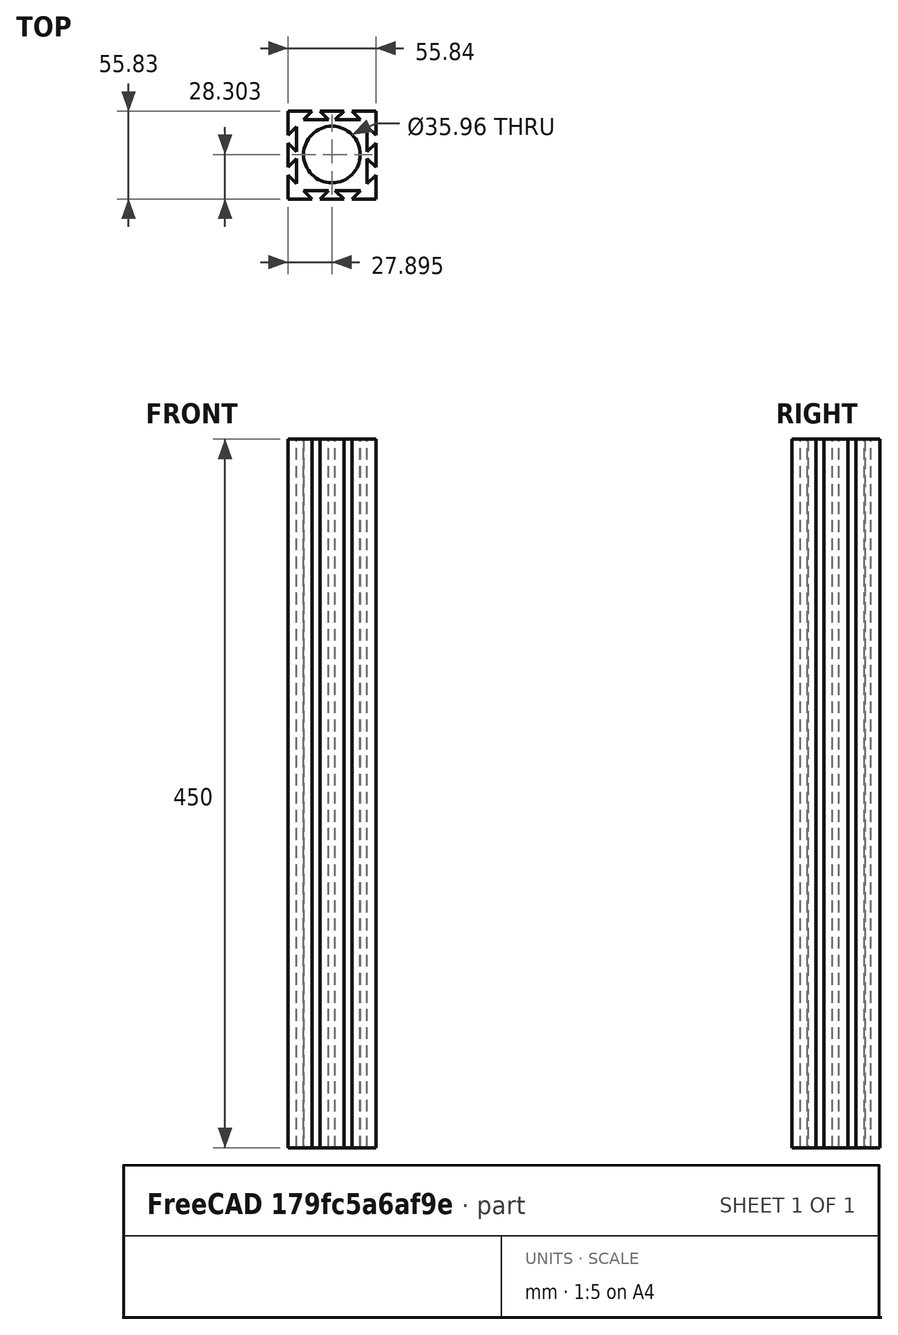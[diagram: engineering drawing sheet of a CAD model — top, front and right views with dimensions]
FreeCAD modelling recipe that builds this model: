
FCSTD DOCUMENT  (FreeCAD 0.18R16110 (Git))
Label: Quadextrusion
License: All rights reserved
LicenseURL: http://en.wikipedia.org/wiki/All_rights_reserved
objects: Sketcher::SketchObject×1, Part::Extrusion×1
note: 2 computed .brp shape members not serialized (recipe doc carries the construction recipe); baked Part::Feature solids carry a one-line shape summary decoded from their .brp

FEATURE [Sketcher::SketchObject] Sketch
  sketch-geometry (62):
    g0: LineSegment StartX=81.5164 StartY=-47.279 StartZ=0 EndX=81.5164 EndY=-62.5946 EndZ=0
    g1: LineSegment StartX=81.5164 StartY=-62.5946 StartZ=0 EndX=66.2008 EndY=-62.5946 EndZ=0
    g2: LineSegment StartX=66.2008 StartY=-62.5946 StartZ=0 EndX=71.7008 EndY=-57.0946 EndZ=0
    g3: LineSegment StartX=71.7008 StartY=-57.0946 StartZ=0 EndX=55.7008 EndY=-57.0946 EndZ=0
    g4: LineSegment StartX=55.7008 StartY=-57.0946 StartZ=0 EndX=61.2008 EndY=-62.5946 EndZ=0
    g5: LineSegment StartX=61.2008 StartY=-62.5946 StartZ=0 EndX=45.9941 EndY=-62.5946 EndZ=0
    g6: LineSegment [constr] StartX=61.2008 StartY=-62.5946 StartZ=0 EndX=66.2008 EndY=-62.5946 EndZ=0
    g7: LineSegment [constr] StartX=55.7008 StartY=-57.0946 StartZ=0 EndX=55.7008 EndY=-62.5946 EndZ=0
    g8: LineSegment StartX=81.5164 StartY=-47.279 StartZ=0 EndX=76.0164 EndY=-52.779 EndZ=0
    g9: LineSegment StartX=76.0164 StartY=-52.779 StartZ=0 EndX=76.0164 EndY=-36.779 EndZ=0
    g10: LineSegment StartX=76.0164 StartY=-36.779 StartZ=0 EndX=81.5164 EndY=-42.279 EndZ=0
    g11: LineSegment StartX=81.5164 StartY=-42.279 StartZ=0 EndX=81.5164 EndY=-27.0723 EndZ=0
    g12: LineSegment StartX=45.9941 StartY=-62.5946 StartZ=0 EndX=51.4941 EndY=-57.0946 EndZ=0
    g13: LineSegment StartX=51.4941 StartY=-57.0946 StartZ=0 EndX=35.4941 EndY=-57.0946 EndZ=0
    g14: LineSegment StartX=35.4941 StartY=-57.0946 StartZ=0 EndX=40.9941 EndY=-62.5946 EndZ=0
    g15: LineSegment StartX=40.9941 StartY=-62.5946 StartZ=0 EndX=25.6785 EndY=-62.5946 EndZ=0
    g16: LineSegment StartX=25.6785 StartY=-62.5946 StartZ=0 EndX=25.6785 EndY=-47.279 EndZ=0
    g17: LineSegment [constr] StartX=35.4941 StartY=-57.0946 StartZ=0 EndX=35.4941 EndY=-62.5946 EndZ=0
    g18: LineSegment [constr] StartX=40.9941 StartY=-62.5946 StartZ=0 EndX=45.9941 EndY=-62.5946 EndZ=0
    g19: LineSegment StartX=81.5164 StartY=-27.0723 StartZ=0 EndX=76.0164 EndY=-32.5723 EndZ=0
    g20: LineSegment StartX=76.0164 StartY=-32.5723 StartZ=0 EndX=76.0164 EndY=-16.5723 EndZ=0
    g21: LineSegment StartX=76.0164 StartY=-16.5723 StartZ=0 EndX=81.5164 EndY=-22.0723 EndZ=0
    g22: LineSegment StartX=81.5164 StartY=-22.0723 StartZ=0 EndX=81.5164 EndY=-6.75669 EndZ=0
    g23: LineSegment StartX=81.5164 StartY=-6.75669 StartZ=0 EndX=66.2008 EndY=-6.75669 EndZ=0
    g24: LineSegment [constr] StartX=81.5164 StartY=-22.0723 StartZ=0 EndX=81.5164 EndY=-27.0723 EndZ=0
    g25: LineSegment [constr] StartX=81.5164 StartY=-42.279 StartZ=0 EndX=81.5164 EndY=-47.279 EndZ=0
    g26: LineSegment [constr] StartX=76.0164 StartY=-52.779 StartZ=0 EndX=81.5164 EndY=-52.779 EndZ=0
    g27: LineSegment StartX=66.2008 StartY=-6.75669 StartZ=0 EndX=71.7008 EndY=-12.2567 EndZ=0
    g28: LineSegment StartX=71.7008 StartY=-12.2567 StartZ=0 EndX=55.7008 EndY=-12.2567 EndZ=0
    g29: LineSegment StartX=55.7008 StartY=-12.2567 StartZ=0 EndX=61.2008 EndY=-6.75669 EndZ=0
    g30: LineSegment StartX=61.2008 StartY=-6.75669 StartZ=0 EndX=45.9941 EndY=-6.75669 EndZ=0
    g31: LineSegment StartX=45.9941 StartY=-6.75669 StartZ=0 EndX=51.4941 EndY=-12.2567 EndZ=0
    g32: LineSegment StartX=51.4941 StartY=-12.2567 StartZ=0 EndX=35.4941 EndY=-12.2567 EndZ=0
    g33: LineSegment StartX=35.4941 StartY=-12.2567 StartZ=0 EndX=40.9941 EndY=-6.75669 EndZ=0
    g34: LineSegment StartX=40.9941 StartY=-6.75669 StartZ=0 EndX=25.6785 EndY=-6.75669 EndZ=0
    g35: LineSegment StartX=25.6785 StartY=-6.75669 StartZ=0 EndX=25.6785 EndY=-22.0723 EndZ=0
    g36: LineSegment [constr] StartX=40.9941 StartY=-6.75669 StartZ=0 EndX=45.9941 EndY=-6.75669 EndZ=0
    g37: LineSegment [constr] StartX=61.2008 StartY=-6.75669 StartZ=0 EndX=66.2008 EndY=-6.75669 EndZ=0
    g38: LineSegment [constr] StartX=51.4941 StartY=-11.727 StartZ=0 EndX=51.4941 EndY=-12.2567 EndZ=0
    g39: LineSegment [constr] StartX=51.4941 StartY=-12.2567 StartZ=0 EndX=51.4941 EndY=-6.75669 EndZ=0
    g40: LineSegment [constr] StartX=71.7008 StartY=-6.75669 StartZ=0 EndX=71.7008 EndY=-12.2567 EndZ=0
    g41: LineSegment StartX=25.6785 StartY=-22.0723 StartZ=0 EndX=31.1785 EndY=-16.5723 EndZ=0
    g42: LineSegment StartX=31.1785 StartY=-16.5723 StartZ=0 EndX=31.1785 EndY=-32.5723 EndZ=0
    g43: LineSegment StartX=31.1785 StartY=-32.5723 StartZ=0 EndX=25.6785 EndY=-27.0723 EndZ=0
    g44: LineSegment StartX=25.6785 StartY=-27.0723 StartZ=0 EndX=25.6785 EndY=-42.279 EndZ=0
    g45: LineSegment StartX=25.6785 StartY=-42.279 StartZ=0 EndX=31.1785 EndY=-36.779 EndZ=0
    g46: LineSegment StartX=31.1785 StartY=-36.779 StartZ=0 EndX=31.1785 EndY=-52.779 EndZ=0
    g47: GeomPoint X=25.6785 Y=-47.279 Z=0
    g48: LineSegment StartX=25.6785 StartY=-47.279 StartZ=0 EndX=31.1785 EndY=-52.779 EndZ=0
    g49: LineSegment [constr] StartX=31.1785 StartY=-16.5723 StartZ=0 EndX=25.6785 EndY=-16.5723 EndZ=0
    g50: LineSegment [constr] StartX=31.1785 StartY=-36.779 StartZ=0 EndX=25.6785 EndY=-36.779 EndZ=0
    g51: LineSegment [constr] StartX=25.6785 StartY=-22.0723 StartZ=0 EndX=25.6785 EndY=-27.0723 EndZ=0
    g52: LineSegment [constr] StartX=25.6785 StartY=-42.279 StartZ=0 EndX=25.6785 EndY=-47.279 EndZ=0
    g53: LineSegment [constr] StartX=31.1785 StartY=-52.779 StartZ=0 EndX=35.4941 EndY=-57.0946 EndZ=0
    g54: LineSegment [constr] StartX=71.7008 StartY=-57.0946 StartZ=0 EndX=76.0164 EndY=-52.779 EndZ=0
    g55: LineSegment [constr] StartX=76.0164 StartY=-16.5723 StartZ=0 EndX=71.7008 EndY=-12.2567 EndZ=0
    g56: LineSegment [constr] StartX=31.1785 StartY=-16.5723 StartZ=0 EndX=35.4941 EndY=-12.2567 EndZ=0
    g57: LineSegment [constr] StartX=31.1785 StartY=-36.779 StartZ=0 EndX=31.1785 EndY=-32.5723 EndZ=0
    g58: LineSegment [constr] StartX=51.4941 StartY=-12.2567 StartZ=0 EndX=55.7008 EndY=-12.2567 EndZ=0
    g59: LineSegment [constr] StartX=51.4941 StartY=-57.0946 StartZ=0 EndX=55.7008 EndY=-57.0946 EndZ=0
    g60: LineSegment [constr] StartX=76.0164 StartY=-32.5723 StartZ=0 EndX=76.0164 EndY=-36.779 EndZ=0
    g61: Circle CenterX=53.5745 CenterY=-34.2866 CenterZ=0 NormalX=0 NormalY=0 NormalZ=1 AngleXU=0 Radius=17.9791
  constraints (168):
    c: Vertical(g0)
    c: Coincident(g0,g1)
    c: Coincident(g2,g3)
    c: Horizontal(g3)
    c: Coincident(g3,g4)
    c: Coincident(g4,g5)
    c: Horizontal(g5)
    c: Coincident(g6,g4)
    c: Coincident(g6,g1)
    c: Distance(g6) = 5
    c: Horizontal(g6)
    c: Coincident(g7,g3)
    c: PointOnObject(g7,g5)
    c: Vertical(g7)
    c: Distance(g7) = 5.5
    c: Angle(g1,g2) = 0.785398
    c: Coincident(g0,g8)
    c: Coincident(g8,g9)
    c: Vertical(g9)
    c: Coincident(g9,g10)
    c: Coincident(g10,g11)
    c: Vertical(g11)
    c: Angle(g8,g0) = 0.785398
    c: Angle(g11,g10) = 0.785398
    c: Coincident(g5,g12)
    c: Coincident(g12,g13)
    c: Horizontal(g13)
    c: Coincident(g13,g14)
    c: Coincident(g14,g15)
    c: Horizontal(g15)
    c: Coincident(g15,g16)
    c: Angle(g14,g15) = 0.785398
    c: Angle(g15,g16) = 1.5708
    c: Coincident(g17,g13)
    c: PointOnObject(g17,g15)
    c: Equal(g7,g17)
    c: Coincident(g18,g14)
    c: Coincident(g18,g5)
    c: Equal(g18,g6)
    c: Perpendicular(g15,g17)
    c: Equal(g2,g4)
    c: Equal(g4,g12)
    c: Equal(g12,g14)
    c: Coincident(g11,g19)
    c: Coincident(g19,g20)
    c: Vertical(g20)
    c: Coincident(g20,g21)
    c: Coincident(g21,g22)
    c: Vertical(g22)
    c: Coincident(g22,g23)
    c: Horizontal(g23)
    c: Angle(g19,g11) = 0.785398
    c: Angle(g22,g21) = 0.785398
    c: Coincident(g24,g21)
    c: Coincident(g24,g11)
    c: Coincident(g25,g10)
    c: Coincident(g25,g0)
    c: Vertical(g25)
    c: Equal(g25,g24)
    c: Distance(g24) = 5
    c: Coincident(g26,g8)
    c: PointOnObject(g26,g0)
    c: Horizontal(g26)
    c: DistanceX(g26,g26) = 5.5
    c: Equal(g24,g25)
    c: Coincident(g23,g27)
    c: Coincident(g27,g28)
    c: Horizontal(g28)
    c: Coincident(g28,g29)
    c: Coincident(g29,g30)
    c: Horizontal(g30)
    c: Coincident(g30,g31)
    c: Coincident(g31,g32)
    c: Horizontal(g32)
    c: Coincident(g32,g33)
    c: Coincident(g33,g34)
    c: Horizontal(g34)
    c: Coincident(g34,g35)
    c: Vertical(g35)
    c: Coincident(g36,g33)
    c: Coincident(g36,g30)
    c: Horizontal(g36)
    c: Coincident(g37,g29)
    c: Coincident(g37,g23)
    c: Horizontal(g37)
    c: Equal(g37,g36)
    c: DistanceX(g37,g37) = 5
    c: Coincident(g38,g31)
    c: Vertical(g38)
    c: Coincident(g39,g31)
    c: PointOnObject(g39,g30)
    c: Vertical(g39)
    c: PointOnObject(g40,g23)
    c: Coincident(g40,g27)
    c: Equal(g40,g39)
    c: DistanceY(g39,g39) = 5.5
    c: Angle(g27,g23) = 0.785398
    c: Angle(g30,g29) = 0.785398
    c: Angle(g31,g30) = 0.785398
    c: Angle(g32,g33) = 0.785398
    c: Coincident(g35,g41)
    c: Coincident(g41,g42)
    c: Vertical(g42)
    c: Coincident(g42,g43)
    c: Coincident(g43,g44)
    c: Coincident(g44,g45)
    c: Coincident(g45,g46)
    c: Vertical(g46)
    c: Coincident(g47,g16)
    c: Coincident(g48,g16)
    c: Coincident(g48,g46)
    c: Angle(g41,g35) = 0.785398
    c: Angle(g44,g43) = 0.785398
    c: Angle(g45,g44) = 0.785398
    c: Angle(g16,g48) = 0.785398
    c: Angle(g45,g46) = 0.785398
    c: Coincident(g49,g41)
    c: PointOnObject(g49,g35)
    c: Horizontal(g49)
    c: Coincident(g50,g45)
    c: PointOnObject(g50,g44)
    c: Horizontal(g50)
    c: DistanceX(g49,g49) = 5.5
    c: Equal(g50,g49)
    c: Coincident(g51,g35)
    c: Coincident(g51,g43)
    c: Coincident(g52,g44)
    c: Coincident(g52,g16)
    c: Vertical(g52)
    c: Equal(g52,g51)
    c: DistanceY(g51,g51) = 5
    c: Equal(g32,g42)
    c: Equal(g42,g28)
    c: Equal(g28,g20)
    c: Equal(g20,g9)
    c: Equal(g9,g3)
    c: Equal(g3,g13)
    c: Equal(g13,g46)
    c: Equal(g0,g1)
    c: Equal(g15,g16)
    c: Equal(g35,g34)
    c: Equal(g23,g22)
    c: Equal(g5,g44)
    c: Equal(g44,g30)
    c: Equal(g30,g11)
    c: Angle(g0,g1) = 1.5708
    c: Coincident(g53,g46)
    c: Coincident(g53,g13)
    c: Coincident(g54,g2)
    c: Coincident(g54,g8)
    c: Coincident(g55,g20)
    c: Coincident(g55,g27)
    c: Coincident(g56,g41)
    c: Coincident(g56,g32)
    c: Equal(g56,g55)
    c: Equal(g55,g54)
    c: Equal(g54,g53)
    c: Coincident(g57,g45)
    c: Coincident(g57,g42)
    c: Coincident(g58,g31)
    c: Coincident(g58,g28)
    c: Coincident(g59,g12)
    c: Coincident(g59,g3)
    c: Coincident(g60,g19)
    c: Coincident(g60,g9)
    c: Equal(g57,g58)
    c: Equal(g58,g60)
    c: Equal(g60,g59)
FEATURE [Part::Extrusion] Extrude
  Base = -> Sketch
  Dir = (0,0,1)
  DirMode = 2
  FaceMakerClass = Part::FaceMakerBullseye
  LengthFwd = 450
  LengthRev = 0
  Solid = true
  Symmetric = false
